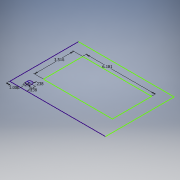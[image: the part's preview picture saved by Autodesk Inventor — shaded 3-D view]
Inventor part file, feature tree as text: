
AUTODESK INVENTOR PART (.ipt)
format: ipt  version: 2019 (Build 230136000, 136)  size: 97,280 bytes
history: native  units: in
note: dims shown in document units (in); Inventor stores cm internally (conversion verified against a paired STEP export)
features: sketch x1
ambient origin geometry x8: Origin, YZ Plane, XZ Plane, XY Plane, X Axis, Y Axis, Z Axis, Center Point
feature tree (1):
  sketch  "Sketch2"  dims[d0=0.4291in d1=0.4724in d2=0.2382in d3=0.2382in d4=0.75in d5=1.0in d6=6.1811in d7=3.5157in]
